# Revit family: Furniture_Shelving&Storage_Sjobergs_Cabinet_3
name_source: partatom
category: Furniture
revit_build: Autodesk Revit 2017 (Build: 20190508_0315(x64)
units: mm (PartAtom-declared; Revit-internal decimal feet)

## family parameters
Always vertical = Yes
Cut with Voids When Loaded = No
OmniClass Number = 23.40.20.27.21
OmniClass Title = Mobile Storage Units
Room Calculation Point = No
Shared = No
Work Plane-Based = No

## types (1)
- 33041 Sjobergs Complete Cabinet 3
    AssetType = Movable
    BIMObjectName = Furniture_Shelving&Storage_Sjobergs_Cabinet_3
    Brand = Sjobergs
    Category = Cabinets
    Collection = Cabinet
    Color = Wooden
    ConvergoRefNr = 0184-2005-0013-SE
    Cost = 0 $
    Description = A sturdy cabinet for student work. Frame and interior in 18 mm birch plywood that provides both stability
    Features = A sturdy cabinet for student work. Frame and interior in 18 mm birch plywood that provides both stability
    Finish = Birch plywood 18 mm, doors in birch laminate
    IfcExportAs = IfcFurnitureType
    IfcExportType = DRAWER
    MainColor = Wooden
    ManufacterURL = https://www.sjobergs.se
    Manufacturer = Sjobergs
    ManufacturerName = Sjobergs
    Material = Wood
    Model = 33041 Sjobergs Complete Cabinet 3
    ModelNumber = 33041
    NBSDescription = Cabinets
    NBSReference = 45-35-47/415
    Name = Sjobergs_Cabinet_3
    NominalDepth = 500 mm  [stored 1.64042 ft]
    NominalHeight = 490 mm  [stored 1.60761 ft]
    NominalWidth = 1000 mm
    ProductDatasheet = https://www.sjobergs.se
    ProductInformation = A sturdy cabinet for student work. Frame and interior in 18 mm birch plywood that provides both stability
    Shape = Sculptured
    Size = 1000x500x490 mm
    URL = https://www.sjobergs.se
    Uniclass2 = Pr_40_30_78_24
    Uniclass2015Description = Storage units
    Uniclass2015Reference = Pr_40_30_78_25
    Version = 1
    VersionDate = 30/06/2020

note: [stored X ft] marks values corroborated as IEEE doubles in the binary element streams (Revit-internal decimal feet)

## geometry (parser evidence)
native form markers: Sweep x6
no freeform markers — native parametric forms only
